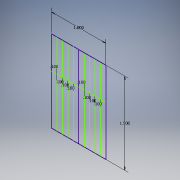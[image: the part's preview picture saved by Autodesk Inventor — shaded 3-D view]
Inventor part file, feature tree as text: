
AUTODESK INVENTOR PART (.ipt)
format: ipt  version: 2016 (Build 200138000, 138)  size: 97,280 bytes
history: native  units: in
note: dims shown in document units (in); Inventor stores cm internally (conversion verified against a paired STEP export)
features: sketch x1
ambient origin geometry x8: Origin, YZ Plane, XZ Plane, XY Plane, X Axis, Y Axis, Z Axis, Center Point
feature tree (1):
  sketch  "Sketch1"  dims[d0=1.0in d1=1.5in d2=0.1in d3=0.1in d4=0.1in d5=0.1in d6=0.1in d7=0.1in d8=0.1in d9=0.1in]
